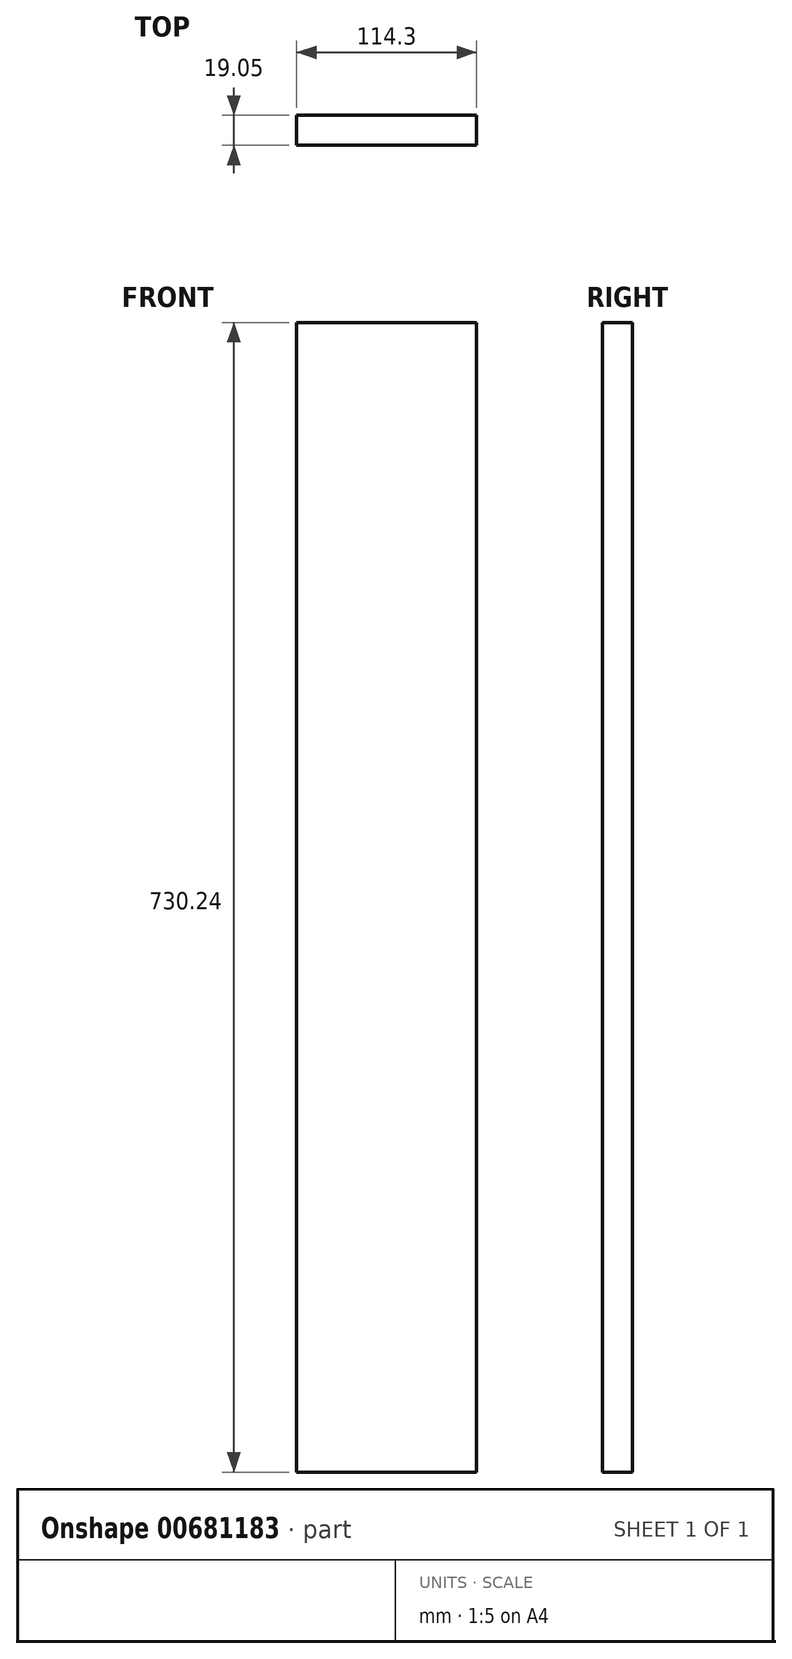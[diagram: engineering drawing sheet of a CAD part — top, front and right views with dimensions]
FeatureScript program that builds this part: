
annotation { "Feature Type Name" : "Feature", "Feature Type Description" : "" }
export const myFeature = defineFeature(function(context is Context, id is Id, definition is map)
    precondition{}
    {
        {
            var Q0;
            Q0=qCreatedBy(makeId("Front.planeOp"),FACE);
            var sketch = newSketch(context, id + "F0", { "sketchPlane" : qUnion([Q0])});
            skLineSegment(sketch, "E0.bottom", {"start": v(57.15, 365.13) * mm, "end": v(-57.15, 365.13) * mm});
            skLineSegment(sketch, "E0.top", {"start": v(57.15, -365.13) * mm, "end": v(-57.15, -365.13) * mm});
            skLineSegment(sketch, "E0.left", {"start": v(57.15, 365.13) * mm, "end": v(57.15, -365.13) * mm});
            skLineSegment(sketch, "E0.right", {"start": v(-57.15, 365.13) * mm, "end": v(-57.15, -365.13) * mm});
            skPoint(sketch, "E0.middle", {"position": v(0, 0) * mm});
            skSolve(sketch);
        }
        {
            var Q0;
            Q0=makeQuery(id+"F0.imprint","IMPRINT",FACE,{"disambiguationData":[TD([[makeQuery(id+"F0.imprint","IMPRINT",EDGE,{"derivedFrom":sQuery(id+"F0.wireOp",EDGE,"E0.bottom")}),1.0]])]});
            extrude(context, id + "F1", {"entities" : qUnion([Q0]), "depth" : 19.05 * mm, "offsetDistance" : 25.4 * mm});
        }
    });
